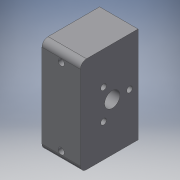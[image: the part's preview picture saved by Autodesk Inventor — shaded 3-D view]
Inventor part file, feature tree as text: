
AUTODESK INVENTOR PART (.ipt)
format: ipt  version: 2019 (Build 230136000, 136)  size: 136,704 bytes
history: native  units: in
note: dims shown in document units (in); Inventor stores cm internally (conversion verified against a paired STEP export)
features: extrude x4, sketch x4, other x2, fillet x1, reference x1, helix x1
ambient origin geometry x8: Origin, YZ Plane, XZ Plane, XY Plane, X Axis, Y Axis, Z Axis, Center Point
bodies: Solid1 (feature_tree)
feature tree (13):
  extrude  "Extrusion1"  Depth=1.9685in
  fillet  "Fillet1"  Radius=0.7874in
  extrude  "Extrusion2"  Depth=0.125in
  extrude  "Extrusion3"  Depth=0.1299in
  extrude  "Extrusion4"  Depth=1.1811in TaperAngle=0.0deg
  sketch  "Sketch1"  dims[d0=1.1811in d1=1.9685in d2=0.7874in d3=0.0in]
  sketch  "Sketch2"  dims[d4=0.125in d5=0.1299in]
  sketch  "Sketch3"  dims[d6=0.1969in d7=0.1299in]
  sketch  "Sketch4"  dims[d8=0.1969in d9=1.1811in d10=0.0in d11=0.315in d12=1.1811in d13=0.0in d14=1.1811in d16=360.0deg d18=1.0in d19=0.0in]
  reference  "Reference1"
  other  "<userpath>\Documents\CAD Files\Helix DLP\Helix DLP Z Stage.iam"
  helix  "Helix DLP Z Stage.iam"  [1 undecoded]
  other  "Z Motor Screw:1"
note: 1 required parameter value undecoded (feature->parameter linkage not recoverable at this tier; creation-order binding heuristic only, values carry confidence <= 0.55)
